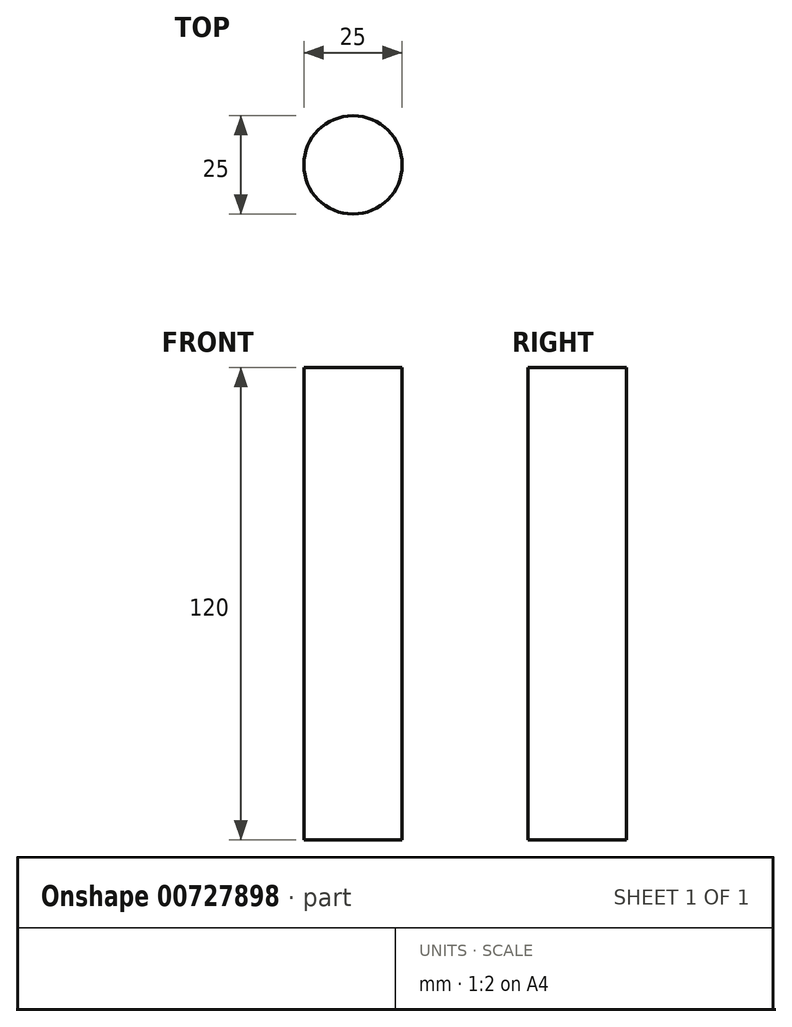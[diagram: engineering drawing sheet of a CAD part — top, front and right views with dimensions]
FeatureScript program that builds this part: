
annotation { "Feature Type Name" : "Feature", "Feature Type Description" : "" }
export const myFeature = defineFeature(function(context is Context, id is Id, definition is map)
    precondition{}
    {
        {
            var Q0;
            Q0=qCreatedBy(makeId("Top.planeOp"),FACE);
            var sketch = newSketch(context, id + "F0", { "sketchPlane" : qUnion([Q0])});
            skCircle(sketch, "E0", {"center": v(0, 0) * mm, "radius": 45 * mm});
            skCircle(sketch, "E1", {"center": v(0, 0) * mm, "radius": 12.5 * mm});
            skLineSegment(sketch, "E2", {"start": v(0, 0) * mm, "end": v(-1500, 0) * mm});
            skLineSegment(sketch, "E3", {"start": v(0, 0) * mm, "end": v(1060.66, -1060.66) * mm});
            skSolve(sketch);
        }
        {
            var Q0;
            Q0=sQuery(id+"F0.wireOp",EDGE,"E1");
            extrude(context, id + "F1", {"bodyType" : ToolBodyType.SURFACE, "surfaceEntities" : qUnion([Q0]), "endBound" : BoundingType.SYMMETRIC, "depth" : 120 * mm, "offsetDistance" : 25 * mm});
        }
    });
